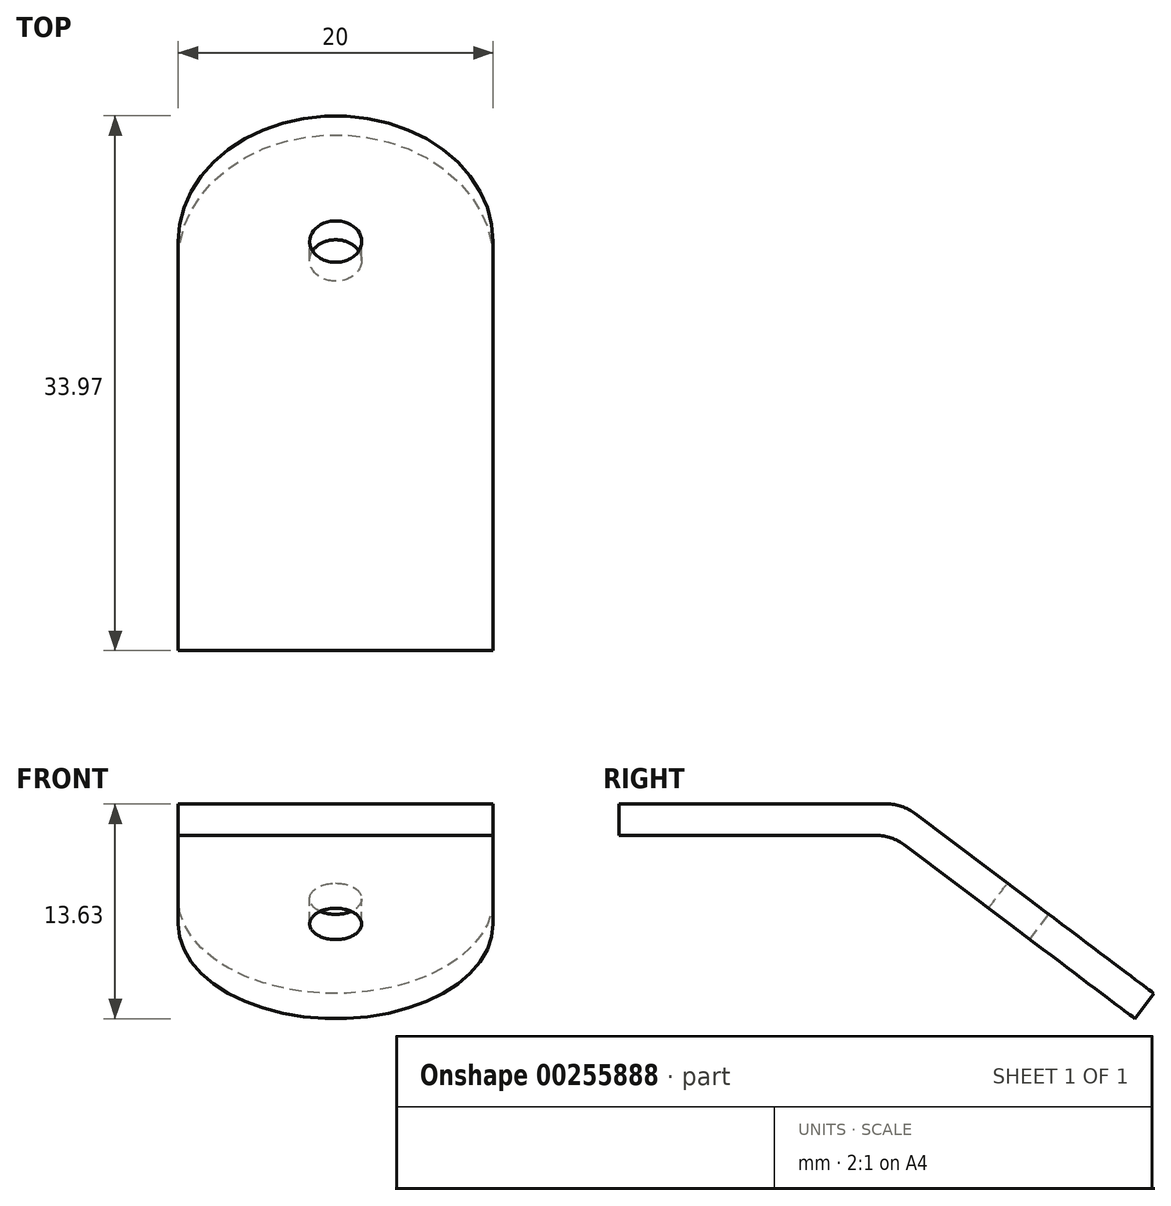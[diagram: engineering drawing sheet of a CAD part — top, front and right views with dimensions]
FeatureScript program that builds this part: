
annotation { "Feature Type Name" : "Feature", "Feature Type Description" : "" }
export const myFeature = defineFeature(function(context is Context, id is Id, definition is map)
    precondition{}
    {
        {
            var Q0;
            Q0=qCreatedBy(makeId("Right.planeOp"),FACE);
            var sketch = newSketch(context, id + "F0", { "sketchPlane" : qUnion([Q0])});
            skLineSegment(sketch, "E0", {"start": v(-27, 33.25) * mm, "end": v(-9, 33.25) * mm});
            skLineSegment(sketch, "E1", {"start": v(-9, 33.25) * mm, "end": v(6.98, 21.22) * mm});
            skLineSegment(sketch, "E2", {"start": v(6.98, 21.22) * mm, "end": v(5.77, 19.62) * mm});
            skLineSegment(sketch, "E3", {"start": v(5.77, 19.62) * mm, "end": v(-9.66, 31.25) * mm});
            skLineSegment(sketch, "E4", {"start": v(-9.66, 31.25) * mm, "end": v(-27, 31.25) * mm});
            skLineSegment(sketch, "E5", {"start": v(-27, 31.25) * mm, "end": v(-27, 33.25) * mm});
            skPoint(sketch, "E6", {"position": v(-18.33, 31.25) * mm});
            skPoint(sketch, "E7", {"position": v(-1.94, 25.44) * mm});
            skSolve(sketch);
        }
        {
            var Q0;
            Q0=makeQuery(id+"F0.imprint","IMPRINT",FACE,{"disambiguationData":[TD([[makeQuery(id+"F0.imprint","IMPRINT",EDGE,{"derivedFrom":sQuery(id+"F0.wireOp",EDGE,"E0")}),-1.0]])]});
            extrude(context, id + "F1", {"entities" : qUnion([Q0]), "depth" : 20 * mm, "symmetric" : true});
        }
        {
            var Q0;
            Q0=makeQuery(id+"F1.opExtrude","SWEPT_FACE",FACE,{"disambiguationData":[OSD([sQuery(id+"F0.wireOp",EDGE,"E1")])]});
            var sketch = newSketch(context, id + "F2", { "sketchPlane" : qUnion([Q0])});
            skLineSegment(sketch, "E8", {"start": v(-10, -7.2) * mm, "end": v(10, -27.2) * mm, "construction": true});
            skPoint(sketch, "E9", {"position": v(0, -17.2) * mm});
            skSolve(sketch);
        }
        {
            var Q0;
            Q0=sQuery(id+"F2.wireOp",VERTEX,"E9");
            var Q1;
            Q1=makeQuery(id+"F1.opExtrude","SWEPT_BODY",BODY,{"disambiguationData":[OSD([sQuery(id+"F0.wireOp",EDGE,"E0"),sQuery(id+"F0.wireOp",EDGE,"E1"),sQuery(id+"F0.wireOp",EDGE,"E2"),sQuery(id+"F0.wireOp",EDGE,"E3"),sQuery(id+"F0.wireOp",EDGE,"E4"),sQuery(id+"F0.wireOp",EDGE,"E5")])]});
            hole(context, id + "F3", {"style" : HoleStyle.SIMPLE, "endStyle" : HoleEndStyle.THROUGH, "holeDiameter" : 3.3 * mm, "tappedDepth" : 12 * mm, "tapClearance" : 3, "startFromSketch" : true, "locations" : qUnion([Q0]), "scope" : qUnion([Q1])});
        }
        {
            var Q0;
            Q0=makeQuery(id+"F1.opExtrude","SWEPT_EDGE",EDGE,{"disambiguationData":[OSD([sQuery(id+"F0.wireOp",EDGE,"E0"),sQuery(id+"F0.wireOp",EDGE,"E1")])]});
            var Q1;
            Q1=makeQuery(id+"F1.opExtrude","SWEPT_EDGE",EDGE,{"disambiguationData":[OSD([sQuery(id+"F0.wireOp",EDGE,"E3"),sQuery(id+"F0.wireOp",EDGE,"E4")])]});
            fillet(context, id + "F4", {"entities" : qUnion([Q0, Q1]), "radius" : 3 * mm, "tangentPropagation" : true, "allowEdgeOverflow" : false});
        }
        {
            var Q0;
            Q0=makeQuery(id+"F1.opExtrude","CAP_EDGE",EDGE,{"disambiguationData":[OSD([sQuery(id+"F0.wireOp",EDGE,"E2")])],"isStart":false});
            var Q1;
            Q1=makeQuery(id+"F1.opExtrude","CAP_EDGE",EDGE,{"disambiguationData":[OSD([sQuery(id+"F0.wireOp",EDGE,"E2")])],"isStart":true});
            fillet(context, id + "F5", {"entities" : qUnion([Q0, Q1]), "radius" : 10 * mm, "tangentPropagation" : true, "allowEdgeOverflow" : false});
        }
    });
